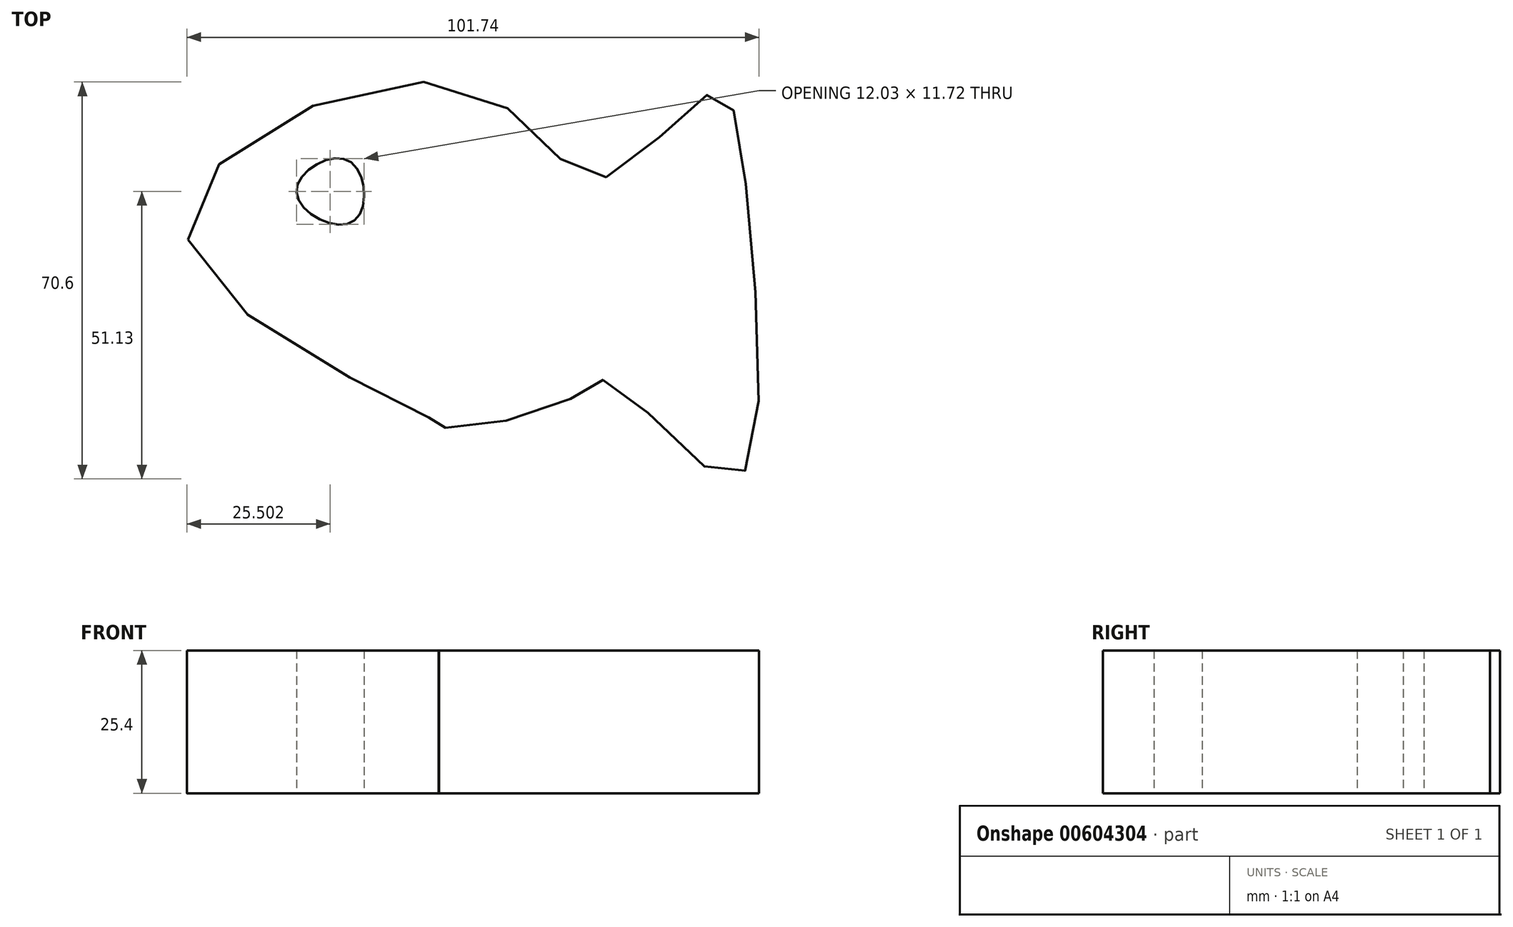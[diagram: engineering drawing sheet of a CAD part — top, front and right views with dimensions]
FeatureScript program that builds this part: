
annotation { "Feature Type Name" : "Feature", "Feature Type Description" : "" }
export const myFeature = defineFeature(function(context is Context, id is Id, definition is map)
    precondition{}
    {
        {
            var Q0;
            Q0=qCreatedBy(makeId("Top.planeOp"),FACE);
            var sketch = newSketch(context, id + "F0", { "sketchPlane" : qUnion([Q0])});
            skFitSpline(sketch, "E0", {"points": [v(-61.24, 11.64) * mm, v(-12.65, 38.95) * mm, v(11.85, 22.49) * mm, v(31.92, 37.75) * mm, v(38.35, 17.27) * mm, v(35.54, -30.92) * mm, v(13.85, -13.65) * mm, v(5.02, -17.67) * mm, v(-16.66, -21.68) * mm, v(-16.66, -21.28) * mm, v(-61.24, 11.64) * mm]});
            skFitSpline(sketch, "E1", {"points": [v(-41.96, 20.08) * mm, v(-31.92, 14.86) * mm, v(-32.73, 25.7) * mm, v(-41.96, 20.08) * mm]});
            skSolve(sketch);
        }
        {
            var Q0;
            Q0=makeQuery(id+"F0.imprint","IMPRINT",FACE,{"disambiguationData":[TD([[makeQuery(id+"F0.imprint","IMPRINT",EDGE,{"derivedFrom":sQuery(id+"F0.wireOp",EDGE,"E0")}),-1.0]])]});
            extrude(context, id + "F1", {"entities" : qUnion([Q0]), "depth" : 25.4 * mm, "offsetDistance" : 25.4 * mm});
        }
    });
